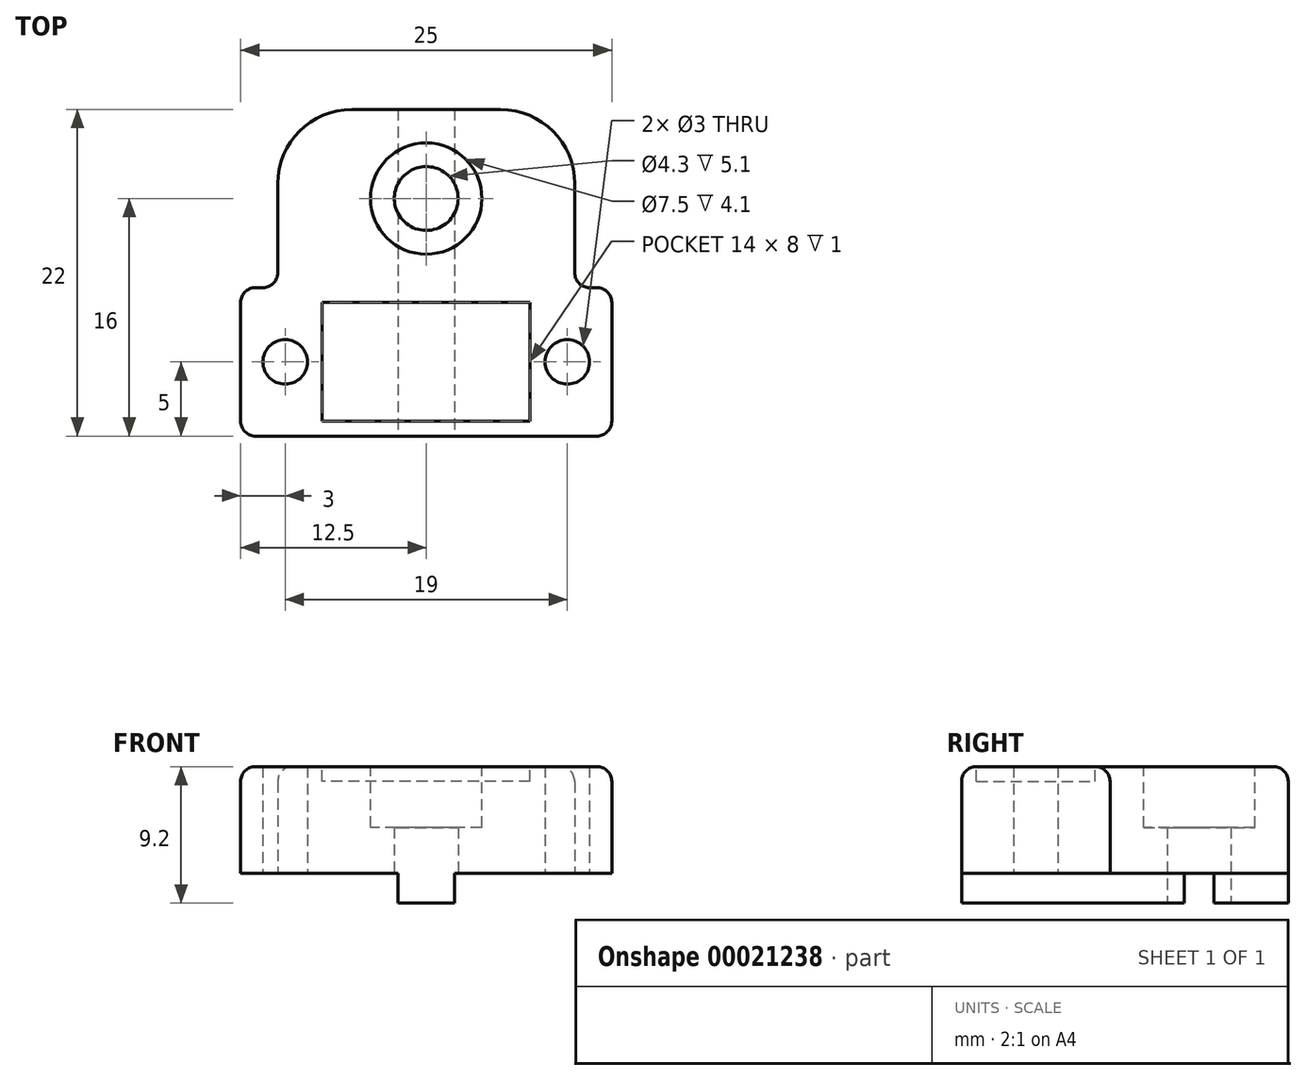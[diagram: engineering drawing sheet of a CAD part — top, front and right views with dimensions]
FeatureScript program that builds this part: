
annotation { "Feature Type Name" : "Feature", "Feature Type Description" : "" }
export const myFeature = defineFeature(function(context is Context, id is Id, definition is map)
    precondition{}
    {
        {
            var Q0;
            Q0=qCreatedBy(makeId("Top.planeOp"),FACE);
            var sketch = newSketch(context, id + "F0", { "sketchPlane" : qUnion([Q0])});
            skLineSegment(sketch, "E0", {"start": v(0, 0) * mm, "end": v(0, 22) * mm, "construction": true});
            skLineSegment(sketch, "E1", {"start": v(0, 0) * mm, "end": v(11.5, 0) * mm});
            skLineSegment(sketch, "E2", {"start": v(12.5, 1) * mm, "end": v(12.5, 9) * mm});
            skLineSegment(sketch, "E3", {"start": v(11.5, 10) * mm, "end": v(11, 10) * mm});
            skLineSegment(sketch, "E4", {"start": v(10, 11) * mm, "end": v(10, 17) * mm});
            skLineSegment(sketch, "E5", {"start": v(5, 22) * mm, "end": v(0, 22) * mm});
            skLineSegment(sketch, "E6.MirrorCS", {"start": v(0, 0) * mm, "end": v(-11.5, 0) * mm});
            skLineSegment(sketch, "E7.MirrorCS", {"start": v(-11.5, 10) * mm, "end": v(-11, 10) * mm});
            skLineSegment(sketch, "E8.MirrorCS", {"start": v(-12.5, 1) * mm, "end": v(-12.5, 9) * mm});
            skLineSegment(sketch, "E9.MirrorCS", {"start": v(-5, 22) * mm, "end": v(0, 22) * mm});
            skLineSegment(sketch, "E10.MirrorCS", {"start": v(-10, 11) * mm, "end": v(-10, 17) * mm});
            skCircle(sketch, "E11", {"center": v(-9.5, 5) * mm, "radius": 1.5 * mm});
            skPoint(sketch, "E11.centerSnap0", {"position": v(-12.5, 5) * mm});
            skCircle(sketch, "E12.MirrorC", {"center": v(9.5, 5) * mm, "radius": 1.5 * mm});
            skCircle(sketch, "E13", {"center": v(0, 16) * mm, "radius": 2.15 * mm});
            skPoint(sketch, "E13.centerSnap0", {"position": v(-10, 16) * mm});
            skPoint(sketch, "E14.visualSharp", {"position": v(-10, 22) * mm});
            skArc(sketch, "E14.filletArc", {"start": v(-5, 22) * mm, "mid": v(-8.54, 20.54) * mm, "end": v(-10, 17) * mm});
            skPoint(sketch, "E15.visualSharp", {"position": v(10, 22) * mm});
            skArc(sketch, "E15.filletArc", {"start": v(10, 17) * mm, "mid": v(8.54, 20.54) * mm, "end": v(5, 22) * mm});
            skPoint(sketch, "E16.visualSharp", {"position": v(10, 10) * mm});
            skArc(sketch, "E16.filletArc", {"start": v(10, 11) * mm, "mid": v(10.3, 10.3) * mm, "end": v(11, 10) * mm});
            skPoint(sketch, "E17.visualSharp", {"position": v(12.5, 10) * mm});
            skArc(sketch, "E17.filletArc", {"start": v(12.5, 9) * mm, "mid": v(12.2, 9.7) * mm, "end": v(11.5, 10) * mm});
            skPoint(sketch, "E18.visualSharp", {"position": v(12.5, 0) * mm});
            skArc(sketch, "E18.filletArc", {"start": v(11.5, 0) * mm, "mid": v(12.2, 0.3) * mm, "end": v(12.5, 1) * mm});
            skPoint(sketch, "E19.visualSharp", {"position": v(-12.5, 0) * mm});
            skArc(sketch, "E19.filletArc", {"start": v(-12.5, 1) * mm, "mid": v(-12.2, 0.3) * mm, "end": v(-11.5, 0) * mm});
            skPoint(sketch, "E20.visualSharp", {"position": v(-10, 10) * mm});
            skArc(sketch, "E20.filletArc", {"start": v(-11, 10) * mm, "mid": v(-10.3, 10.3) * mm, "end": v(-10, 11) * mm});
            skPoint(sketch, "E21.visualSharp", {"position": v(-12.5, 10) * mm});
            skArc(sketch, "E21.filletArc", {"start": v(-11.5, 10) * mm, "mid": v(-12.2, 9.7) * mm, "end": v(-12.5, 9) * mm});
            skSolve(sketch);
        }
        {
            var Q0;
            Q0=makeQuery(id+"F0.imprint","IMPRINT",FACE,{"disambiguationData":[TD([[makeQuery(id+"F0.imprint","IMPRINT",EDGE,{"derivedFrom":sQuery(id+"F0.wireOp",EDGE,"E1")}),1.0]])]});
            extrude(context, id + "F1", {"entities" : qUnion([Q0]), "depth" : (12.5 - 5.3) * mm});
        }
        {
            var Q0;
            Q0=makeQuery(id+"F1.opExtrude","CAP_FACE",FACE,{"disambiguationData":[OSD([sQuery(id+"F0.wireOp",EDGE,"E1"),sQuery(id+"F0.wireOp",EDGE,"E2"),sQuery(id+"F0.wireOp",EDGE,"E3"),sQuery(id+"F0.wireOp",EDGE,"E4"),sQuery(id+"F0.wireOp",EDGE,"E5"),sQuery(id+"F0.wireOp",EDGE,"E6.MirrorCS"),sQuery(id+"F0.wireOp",EDGE,"E7.MirrorCS"),sQuery(id+"F0.wireOp",EDGE,"E8.MirrorCS"),sQuery(id+"F0.wireOp",EDGE,"E9.MirrorCS"),sQuery(id+"F0.wireOp",EDGE,"E10.MirrorCS"),sQuery(id+"F0.wireOp",EDGE,"E11"),sQuery(id+"F0.wireOp",EDGE,"E12.MirrorC"),sQuery(id+"F0.wireOp",EDGE,"E13"),sQuery(id+"F0.wireOp",EDGE,"E14.filletArc"),sQuery(id+"F0.wireOp",EDGE,"E15.filletArc"),sQuery(id+"F0.wireOp",EDGE,"E16.filletArc"),sQuery(id+"F0.wireOp",EDGE,"E17.filletArc"),sQuery(id+"F0.wireOp",EDGE,"E18.filletArc"),sQuery(id+"F0.wireOp",EDGE,"E19.filletArc"),sQuery(id+"F0.wireOp",EDGE,"E20.filletArc"),sQuery(id+"F0.wireOp",EDGE,"E21.filletArc")])],"isStart":false});
            var sketch = newSketch(context, id + "F2", { "sketchPlane" : qUnion([Q0])});
            skCircle(sketch, "E22.0", {"center": v(-9.5, 5) * mm, "radius": 1.5 * mm, "construction": true});
            skCircle(sketch, "E22.1", {"center": v(9.5, 5) * mm, "radius": 1.5 * mm, "construction": true});
            skLineSegment(sketch, "E22.2", {"start": v(11.5, 0) * mm, "end": v(-11.5, 0) * mm, "construction": true});
            skCircle(sketch, "E22.3", {"center": v(0, 16) * mm, "radius": 2.15 * mm, "construction": true});
            skLineSegment(sketch, "E23", {"start": v(-11, 10) * mm, "end": v(11, 10) * mm, "construction": true});
            skLineSegment(sketch, "E24.rect.bottom", {"start": v(7, 1) * mm, "end": v(-7, 1) * mm});
            skLineSegment(sketch, "E24.rect.top", {"start": v(7, 9) * mm, "end": v(-7, 9) * mm});
            skLineSegment(sketch, "E24.rect.left", {"start": v(7, 1) * mm, "end": v(7, 9) * mm});
            skLineSegment(sketch, "E24.rect.right", {"start": v(-7, 1) * mm, "end": v(-7, 9) * mm});
            skPoint(sketch, "E24.rect.middle", {"position": v(0, 5) * mm});
            skCircle(sketch, "E25", {"center": v(0, 16) * mm, "radius": 3.75 * mm});
            skSolve(sketch);
        }
        {
            var Q0;
            Q0=makeQuery(id+"F2.imprint","IMPRINT",FACE,{"disambiguationData":[TD([[makeQuery(id+"F2.imprint","IMPRINT",EDGE,{"derivedFrom":sQuery(id+"F2.wireOp",EDGE,"E24.rect.bottom")}),-1.0]])]});
            extrude(context, id + "F3", {"entities" : qUnion([Q0]), "operationType" : NewBodyOperationType.REMOVE, "oppositeDirection" : true, "depth" : 1 * mm});
        }
        {
            var Q0;
            Q0=makeQuery(id+"F2.imprint","IMPRINT",FACE,{"disambiguationData":[TD([[makeQuery(id+"F2.imprint","IMPRINT",EDGE,{"derivedFrom":sQuery(id+"F2.wireOp",EDGE,"E25")}),1.0]])]});
            extrude(context, id + "F4", {"entities" : qUnion([Q0]), "operationType" : NewBodyOperationType.REMOVE, "oppositeDirection" : true, "depth" : 4.1 * mm});
        }
        {
            var Q0;
            Q0=makeQuery(id+"F1.opExtrude","CAP_EDGE",EDGE,{"disambiguationData":[OSD([sQuery(id+"F0.wireOp",EDGE,"E5"),sQuery(id+"F0.wireOp",EDGE,"E9.MirrorCS")])],"isStart":false});
            fillet(context, id + "F5", {"entities" : qUnion([Q0]), "radius" : 1 * mm, "tangentPropagation" : true, "allowEdgeOverflow" : false});
        }
        {
            var Q0;
            Q0=makeQuery(id+"F1.opExtrude","CAP_FACE",FACE,{"disambiguationData":[OSD([sQuery(id+"F0.wireOp",EDGE,"E1"),sQuery(id+"F0.wireOp",EDGE,"E2"),sQuery(id+"F0.wireOp",EDGE,"E3"),sQuery(id+"F0.wireOp",EDGE,"E4"),sQuery(id+"F0.wireOp",EDGE,"E5"),sQuery(id+"F0.wireOp",EDGE,"E6.MirrorCS"),sQuery(id+"F0.wireOp",EDGE,"E7.MirrorCS"),sQuery(id+"F0.wireOp",EDGE,"E8.MirrorCS"),sQuery(id+"F0.wireOp",EDGE,"E9.MirrorCS"),sQuery(id+"F0.wireOp",EDGE,"E10.MirrorCS"),sQuery(id+"F0.wireOp",EDGE,"E11"),sQuery(id+"F0.wireOp",EDGE,"E12.MirrorC"),sQuery(id+"F0.wireOp",EDGE,"E13"),sQuery(id+"F0.wireOp",EDGE,"E14.filletArc"),sQuery(id+"F0.wireOp",EDGE,"E15.filletArc"),sQuery(id+"F0.wireOp",EDGE,"E16.filletArc"),sQuery(id+"F0.wireOp",EDGE,"E17.filletArc"),sQuery(id+"F0.wireOp",EDGE,"E18.filletArc"),sQuery(id+"F0.wireOp",EDGE,"E19.filletArc"),sQuery(id+"F0.wireOp",EDGE,"E20.filletArc"),sQuery(id+"F0.wireOp",EDGE,"E21.filletArc")])],"isStart":true});
            var sketch = newSketch(context, id + "F6", { "sketchPlane" : qUnion([Q0])});
            skLineSegment(sketch, "E26", {"start": v(0, -22) * mm, "end": v(0, 0) * mm, "construction": true});
            skLineSegment(sketch, "E27", {"start": v(1.9, -22) * mm, "end": v(1.9, 0) * mm});
            skLineSegment(sketch, "E28.MirrorCS", {"start": v(-1.9, -22) * mm, "end": v(-1.9, 0) * mm});
            skLineSegment(sketch, "E29", {"start": v(1.9, -22) * mm, "end": v(-1.9, -22) * mm});
            skLineSegment(sketch, "E30", {"start": v(1.9, 0) * mm, "end": v(-1.9, 0) * mm});
            skSolve(sketch);
        }
        {
            var Q0;
            {var subQ0=sQuery(id+"F6.wireOp",EDGE,"E29");Q0=makeQuery(id+"F6.imprint","IMPRINT",FACE,{"disambiguationData":[TD([[makeQuery(id+"F6.imprint","IMPRINT",EDGE,{"derivedFrom":subQ0}),-1.0]])]});}
            var Q1;
            {var subQ4=sQuery(id+"F6.wireOp",EDGE,"E30");Q1=makeQuery(id+"F6.imprint","IMPRINT",FACE,{"disambiguationData":[TD([[makeQuery(id+"F6.imprint","IMPRINT",EDGE,{"derivedFrom":subQ4}),1.0]])]});}
            extrude(context, id + "F7", {"entities" : qUnion([Q0, Q1]), "operationType" : NewBodyOperationType.ADD, "depth" : 2 * mm});
        }
    });
